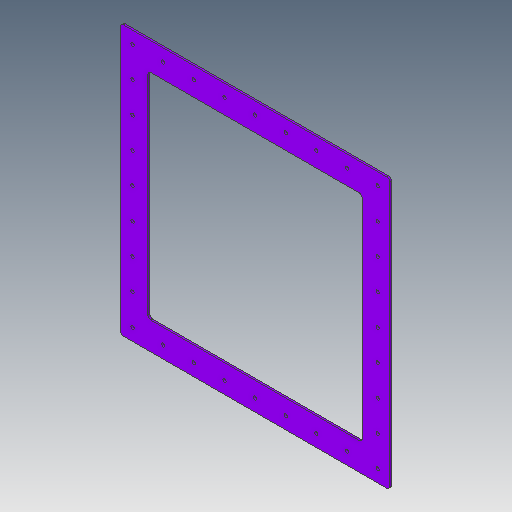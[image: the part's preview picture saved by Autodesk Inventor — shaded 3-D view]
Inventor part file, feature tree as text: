
AUTODESK INVENTOR PART (.ipt)
format: ipt  version: 2017 (Build 210142000, 142)  size: 200,192 bytes
history: native  units: mm
features: extrude x1
ambient origin geometry x8: Origin, YZ Plane, XZ Plane, XY Plane, X Axis, Y Axis, Z Axis, Center Point
bodies: Body1 (feature_tree)
feature tree (1):
  extrude  "Extrusion3"  Depth=440.0mm
